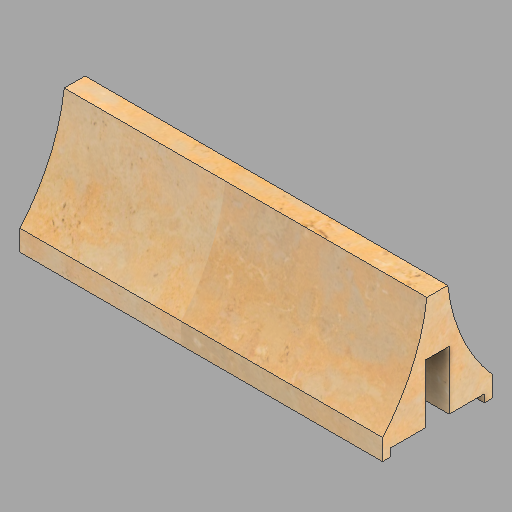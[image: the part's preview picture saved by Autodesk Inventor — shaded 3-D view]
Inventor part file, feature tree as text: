
AUTODESK INVENTOR PART (.ipt)
format: ipt  version: 2022.2 (Build 262287010, 287A)  size: 317,440 bytes
history: native  units: in
note: dims shown in document units (in); Inventor stores cm internally (conversion verified against a paired STEP export)
features: revolve x2, other x1, direct_edit x1
ambient origin geometry x8: Origin, YZ Plane, XZ Plane, XY Plane, X Axis, Y Axis, Z Axis, Center Point
bodies: Solid1 (feature_tree)
feature tree (4):
  other  "Upper Mull (2)"
  direct_edit  "Direct Edit1"
  revolve  "Rotate1"  [1 undecoded]
  revolve  "Rotate2"  Angle=180.0deg
note: 1 required parameter value undecoded (feature->parameter linkage not recoverable at this tier; creation-order binding heuristic only, values carry confidence <= 0.55)
